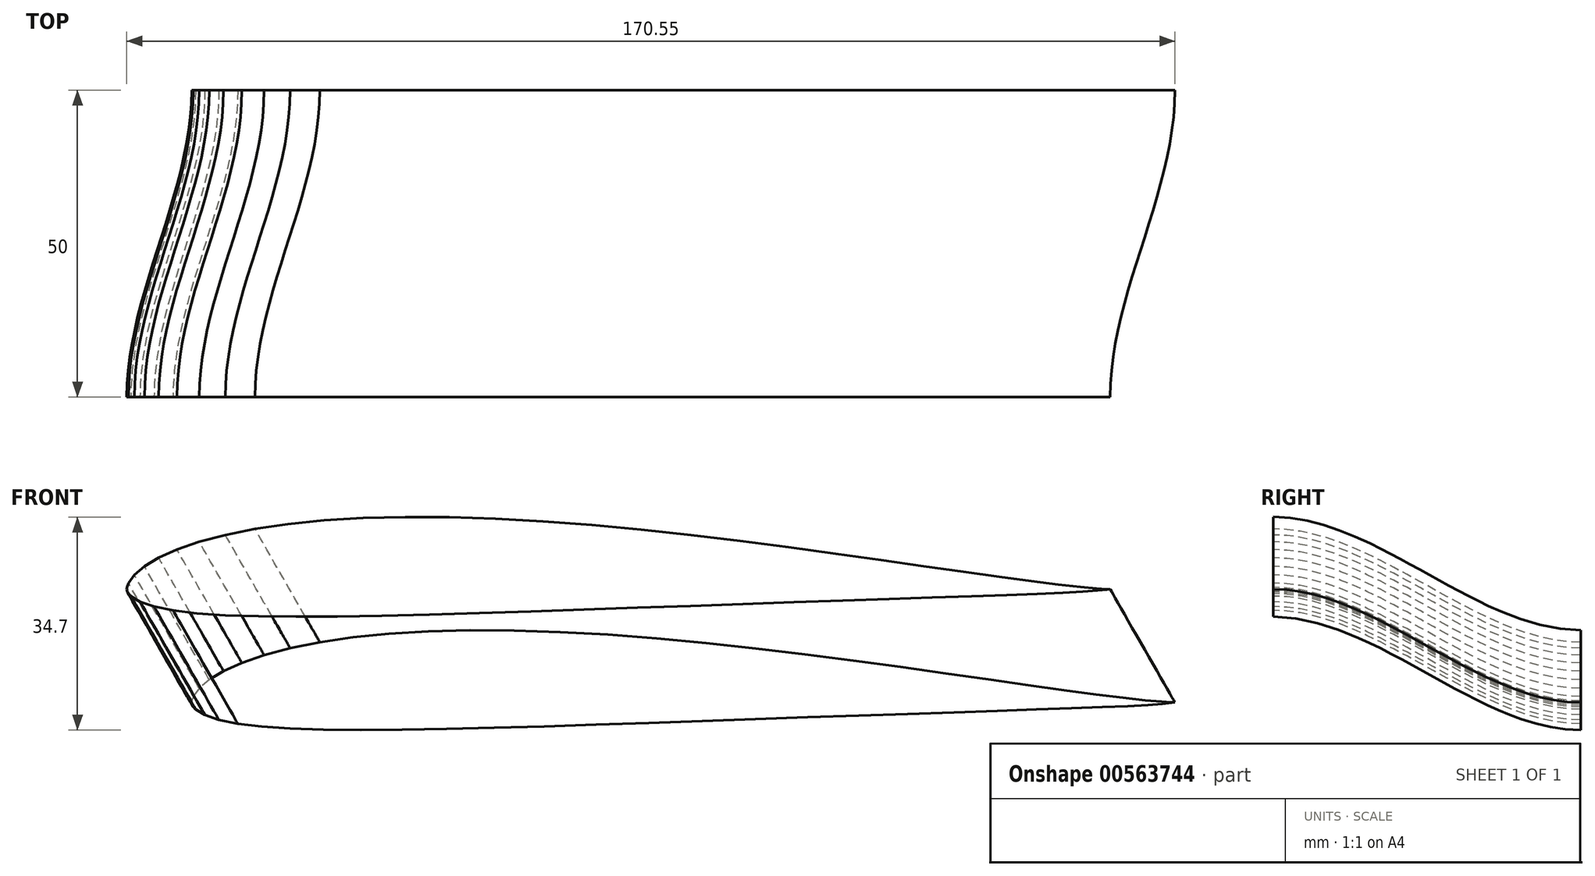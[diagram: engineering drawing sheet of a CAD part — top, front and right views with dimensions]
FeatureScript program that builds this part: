
annotation { "Feature Type Name" : "Feature", "Feature Type Description" : "" }
export const myFeature = defineFeature(function(context is Context, id is Id, definition is map)
    precondition{}
    {
        {
            var Q0;
            Q0=qCreatedBy(makeId("Front.planeOp"),FACE);
            var sketch = newSketch(context, id + "F0", { "sketchPlane" : qUnion([Q0])});
            skLineSegment(sketch, "E0", {"start": v(160, 0) * mm, "end": v(159.44, 0.02) * mm});
            skLineSegment(sketch, "E1", {"start": v(159.44, 0.02) * mm, "end": v(157.8, 0.13) * mm});
            skLineSegment(sketch, "E2", {"start": v(157.8, 0.13) * mm, "end": v(155.15, 0.37) * mm});
            skLineSegment(sketch, "E3", {"start": v(155.15, 0.37) * mm, "end": v(151.57, 0.77) * mm});
            skLineSegment(sketch, "E4", {"start": v(151.57, 0.77) * mm, "end": v(147.15, 1.32) * mm});
            skLineSegment(sketch, "E5", {"start": v(147.15, 1.32) * mm, "end": v(141.96, 2.02) * mm});
            skLineSegment(sketch, "E6", {"start": v(141.96, 2.02) * mm, "end": v(136.1, 2.84) * mm});
            skLineSegment(sketch, "E7", {"start": v(136.1, 2.84) * mm, "end": v(129.65, 3.76) * mm});
            skLineSegment(sketch, "E8", {"start": v(129.65, 3.76) * mm, "end": v(122.7, 4.75) * mm});
            skLineSegment(sketch, "E9", {"start": v(122.7, 4.75) * mm, "end": v(115.35, 5.79) * mm});
            skLineSegment(sketch, "E10", {"start": v(115.35, 5.79) * mm, "end": v(107.68, 6.83) * mm});
            skLineSegment(sketch, "E11", {"start": v(107.68, 6.83) * mm, "end": v(99.8, 7.85) * mm});
            skLineSegment(sketch, "E12", {"start": v(99.8, 7.85) * mm, "end": v(91.77, 8.82) * mm});
            skLineSegment(sketch, "E13", {"start": v(91.77, 8.82) * mm, "end": v(83.69, 9.69) * mm});
            skLineSegment(sketch, "E14", {"start": v(83.69, 9.69) * mm, "end": v(75.64, 10.44) * mm});
            skLineSegment(sketch, "E15", {"start": v(75.64, 10.44) * mm, "end": v(67.7, 11.05) * mm});
            skLineSegment(sketch, "E16", {"start": v(67.7, 11.05) * mm, "end": v(59.96, 11.48) * mm});
            skLineSegment(sketch, "E17", {"start": v(59.96, 11.48) * mm, "end": v(52.46, 11.73) * mm});
            skLineSegment(sketch, "E18", {"start": v(52.46, 11.73) * mm, "end": v(45.28, 11.77) * mm});
            skLineSegment(sketch, "E19", {"start": v(45.28, 11.77) * mm, "end": v(38.48, 11.6) * mm});
            skLineSegment(sketch, "E20", {"start": v(38.48, 11.6) * mm, "end": v(32.12, 11.22) * mm});
            skLineSegment(sketch, "E21", {"start": v(32.12, 11.22) * mm, "end": v(26.23, 10.63) * mm});
            skLineSegment(sketch, "E22", {"start": v(26.23, 10.63) * mm, "end": v(20.86, 9.83) * mm});
            skLineSegment(sketch, "E23", {"start": v(20.86, 9.83) * mm, "end": v(16.04, 8.85) * mm});
            skLineSegment(sketch, "E24", {"start": v(16.04, 8.85) * mm, "end": v(11.8, 7.71) * mm});
            skLineSegment(sketch, "E25", {"start": v(11.8, 7.71) * mm, "end": v(8.18, 6.45) * mm});
            skLineSegment(sketch, "E26", {"start": v(8.18, 6.45) * mm, "end": v(5.2, 5.11) * mm});
            skLineSegment(sketch, "E27", {"start": v(5.2, 5.11) * mm, "end": v(2.87, 3.72) * mm});
            skLineSegment(sketch, "E28", {"start": v(2.87, 3.72) * mm, "end": v(1.23, 2.33) * mm});
            skLineSegment(sketch, "E29", {"start": v(1.23, 2.33) * mm, "end": v(0.27, 1) * mm});
            skLineSegment(sketch, "E30", {"start": v(0.27, 1) * mm, "end": v(0.03, 0.3) * mm});
            skLineSegment(sketch, "E31", {"start": v(0.03, 0.3) * mm, "end": v(0, 0.02) * mm});
            skLineSegment(sketch, "E32", {"start": v(0, 0.02) * mm, "end": v(0.02, -0.23) * mm});
            skLineSegment(sketch, "E33", {"start": v(0.02, -0.23) * mm, "end": v(0.11, -0.47) * mm});
            skLineSegment(sketch, "E34", {"start": v(0.11, -0.47) * mm, "end": v(0.27, -0.71) * mm});
            skLineSegment(sketch, "E35", {"start": v(0.27, -0.71) * mm, "end": v(0.66, -1.13) * mm});
            skLineSegment(sketch, "E36", {"start": v(0.66, -1.13) * mm, "end": v(2.15, -2.03) * mm});
            skLineSegment(sketch, "E37", {"start": v(2.15, -2.03) * mm, "end": v(4.44, -2.82) * mm});
            skLineSegment(sketch, "E38", {"start": v(4.44, -2.82) * mm, "end": v(7.52, -3.45) * mm});
            skLineSegment(sketch, "E39", {"start": v(7.52, -3.45) * mm, "end": v(11.4, -3.92) * mm});
            skLineSegment(sketch, "E40", {"start": v(11.4, -3.92) * mm, "end": v(16.05, -4.23) * mm});
            skLineSegment(sketch, "E41", {"start": v(16.05, -4.23) * mm, "end": v(21.44, -4.42) * mm});
            skLineSegment(sketch, "E42", {"start": v(21.44, -4.42) * mm, "end": v(27.52, -4.48) * mm});
            skLineSegment(sketch, "E43", {"start": v(27.52, -4.48) * mm, "end": v(34.24, -4.43) * mm});
            skLineSegment(sketch, "E44", {"start": v(34.24, -4.43) * mm, "end": v(41.5, -4.31) * mm});
            skLineSegment(sketch, "E45", {"start": v(41.5, -4.31) * mm, "end": v(49.25, -4.12) * mm});
            skLineSegment(sketch, "E46", {"start": v(49.25, -4.12) * mm, "end": v(57.38, -3.88) * mm});
            skLineSegment(sketch, "E47", {"start": v(57.38, -3.88) * mm, "end": v(65.8, -3.61) * mm});
            skLineSegment(sketch, "E48", {"start": v(65.8, -3.61) * mm, "end": v(74.4, -3.32) * mm});
            skLineSegment(sketch, "E49", {"start": v(74.4, -3.32) * mm, "end": v(83.07, -3.01) * mm});
            skLineSegment(sketch, "E50", {"start": v(83.07, -3.01) * mm, "end": v(91.73, -2.7) * mm});
            skLineSegment(sketch, "E51", {"start": v(91.73, -2.7) * mm, "end": v(100.26, -2.4) * mm});
            skLineSegment(sketch, "E52", {"start": v(100.26, -2.4) * mm, "end": v(108.55, -2.12) * mm});
            skLineSegment(sketch, "E53", {"start": v(108.55, -2.12) * mm, "end": v(116.52, -1.85) * mm});
            skLineSegment(sketch, "E54", {"start": v(116.52, -1.85) * mm, "end": v(124.05, -1.6) * mm});
            skLineSegment(sketch, "E55", {"start": v(124.05, -1.6) * mm, "end": v(131.06, -1.36) * mm});
            skLineSegment(sketch, "E56", {"start": v(131.06, -1.36) * mm, "end": v(137.47, -1.14) * mm});
            skLineSegment(sketch, "E57", {"start": v(137.47, -1.14) * mm, "end": v(143.18, -0.94) * mm});
            skLineSegment(sketch, "E58", {"start": v(143.18, -0.94) * mm, "end": v(148.15, -0.75) * mm});
            skLineSegment(sketch, "E59", {"start": v(148.15, -0.75) * mm, "end": v(152.3, -0.58) * mm});
            skLineSegment(sketch, "E60", {"start": v(152.3, -0.58) * mm, "end": v(155.57, -0.4) * mm});
            skLineSegment(sketch, "E61", {"start": v(155.57, -0.4) * mm, "end": v(157.96, -0.22) * mm});
            skLineSegment(sketch, "E62", {"start": v(157.96, -0.22) * mm, "end": v(159.47, -0.06) * mm});
            skLineSegment(sketch, "E63", {"start": v(159.47, -0.06) * mm, "end": v(160, 0) * mm});
            skSolve(sketch);
        }
        {
            var Q0;
            Q0=qCreatedBy(makeId("Front.planeOp"),FACE);
            cPlane(context, id + "F1", {"entities" : qUnion([Q0]), "cplaneType" : CPlaneType.OFFSET, "offset" : 50 * mm, "width" : 150 * mm, "height" : 150 * mm});
        }
        {
            var Q0;
            Q0=qCreatedBy(id+"F1.planeOp",FACE);
            var sketch = newSketch(context, id + "F2", { "sketchPlane" : qUnion([Q0])});
            skLineSegment(sketch, "E64", {"start": v(149.45, 18.45) * mm, "end": v(148.89, 18.47) * mm});
            skLineSegment(sketch, "E65", {"start": v(148.89, 18.47) * mm, "end": v(147.25, 18.58) * mm});
            skLineSegment(sketch, "E66", {"start": v(147.25, 18.58) * mm, "end": v(144.6, 18.82) * mm});
            skLineSegment(sketch, "E67", {"start": v(144.6, 18.82) * mm, "end": v(141.02, 19.22) * mm});
            skLineSegment(sketch, "E68", {"start": v(141.02, 19.22) * mm, "end": v(136.6, 19.77) * mm});
            skLineSegment(sketch, "E69", {"start": v(136.6, 19.77) * mm, "end": v(131.4, 20.47) * mm});
            skLineSegment(sketch, "E70", {"start": v(131.4, 20.47) * mm, "end": v(125.54, 21.29) * mm});
            skLineSegment(sketch, "E71", {"start": v(125.54, 21.29) * mm, "end": v(119.1, 22.21) * mm});
            skLineSegment(sketch, "E72", {"start": v(119.1, 22.21) * mm, "end": v(112.15, 23.2) * mm});
            skLineSegment(sketch, "E73", {"start": v(112.15, 23.2) * mm, "end": v(104.8, 24.24) * mm});
            skLineSegment(sketch, "E74", {"start": v(104.8, 24.24) * mm, "end": v(97.13, 25.28) * mm});
            skLineSegment(sketch, "E75", {"start": v(97.13, 25.28) * mm, "end": v(89.24, 26.3) * mm});
            skLineSegment(sketch, "E76", {"start": v(89.24, 26.3) * mm, "end": v(81.21, 27.27) * mm});
            skLineSegment(sketch, "E77", {"start": v(81.21, 27.27) * mm, "end": v(73.14, 28.14) * mm});
            skLineSegment(sketch, "E78", {"start": v(73.14, 28.14) * mm, "end": v(65.1, 28.9) * mm});
            skLineSegment(sketch, "E79", {"start": v(65.1, 28.9) * mm, "end": v(57.16, 29.5) * mm});
            skLineSegment(sketch, "E80", {"start": v(57.16, 29.5) * mm, "end": v(49.4, 29.93) * mm});
            skLineSegment(sketch, "E81", {"start": v(49.4, 29.93) * mm, "end": v(41.9, 30.18) * mm});
            skLineSegment(sketch, "E82", {"start": v(41.9, 30.18) * mm, "end": v(34.73, 30.22) * mm});
            skLineSegment(sketch, "E83", {"start": v(34.73, 30.22) * mm, "end": v(27.93, 30.06) * mm});
            skLineSegment(sketch, "E84", {"start": v(27.93, 30.06) * mm, "end": v(21.56, 29.67) * mm});
            skLineSegment(sketch, "E85", {"start": v(21.56, 29.67) * mm, "end": v(15.68, 29.08) * mm});
            skLineSegment(sketch, "E86", {"start": v(15.68, 29.08) * mm, "end": v(10.3, 28.28) * mm});
            skLineSegment(sketch, "E87", {"start": v(10.3, 28.28) * mm, "end": v(5.48, 27.3) * mm});
            skLineSegment(sketch, "E88", {"start": v(5.48, 27.3) * mm, "end": v(1.25, 26.16) * mm});
            skLineSegment(sketch, "E89", {"start": v(1.25, 26.16) * mm, "end": v(-2.38, 24.9) * mm});
            skLineSegment(sketch, "E90", {"start": v(-2.38, 24.9) * mm, "end": v(-5.36, 23.56) * mm});
            skLineSegment(sketch, "E91", {"start": v(-5.36, 23.56) * mm, "end": v(-7.68, 22.17) * mm});
            skLineSegment(sketch, "E92", {"start": v(-7.68, 22.17) * mm, "end": v(-9.32, 20.78) * mm});
            skLineSegment(sketch, "E93", {"start": v(-9.32, 20.78) * mm, "end": v(-10.28, 19.45) * mm});
            skLineSegment(sketch, "E94", {"start": v(-10.28, 19.45) * mm, "end": v(-10.52, 18.75) * mm});
            skLineSegment(sketch, "E95", {"start": v(-10.52, 18.75) * mm, "end": v(-10.55, 18.47) * mm});
            skLineSegment(sketch, "E96", {"start": v(-10.55, 18.47) * mm, "end": v(-10.53, 18.22) * mm});
            skLineSegment(sketch, "E97", {"start": v(-10.53, 18.22) * mm, "end": v(-10.44, 17.98) * mm});
            skLineSegment(sketch, "E98", {"start": v(-10.44, 17.98) * mm, "end": v(-10.28, 17.74) * mm});
            skLineSegment(sketch, "E99", {"start": v(-10.28, 17.74) * mm, "end": v(-9.9, 17.32) * mm});
            skLineSegment(sketch, "E100", {"start": v(-9.9, 17.32) * mm, "end": v(-8.4, 16.42) * mm});
            skLineSegment(sketch, "E101", {"start": v(-8.4, 16.42) * mm, "end": v(-6.11, 15.63) * mm});
            skLineSegment(sketch, "E102", {"start": v(-6.11, 15.63) * mm, "end": v(-3.03, 15) * mm});
            skLineSegment(sketch, "E103", {"start": v(-3.03, 15) * mm, "end": v(0.84, 14.53) * mm});
            skLineSegment(sketch, "E104", {"start": v(0.84, 14.53) * mm, "end": v(5.5, 14.22) * mm});
            skLineSegment(sketch, "E105", {"start": v(5.5, 14.22) * mm, "end": v(10.89, 14.03) * mm});
            skLineSegment(sketch, "E106", {"start": v(10.89, 14.03) * mm, "end": v(16.97, 13.98) * mm});
            skLineSegment(sketch, "E107", {"start": v(16.97, 13.98) * mm, "end": v(23.68, 14.02) * mm});
            skLineSegment(sketch, "E108", {"start": v(23.68, 14.02) * mm, "end": v(30.96, 14.14) * mm});
            skLineSegment(sketch, "E109", {"start": v(30.96, 14.14) * mm, "end": v(38.7, 14.33) * mm});
            skLineSegment(sketch, "E110", {"start": v(38.7, 14.33) * mm, "end": v(46.83, 14.57) * mm});
            skLineSegment(sketch, "E111", {"start": v(46.83, 14.57) * mm, "end": v(55.24, 14.84) * mm});
            skLineSegment(sketch, "E112", {"start": v(55.24, 14.84) * mm, "end": v(63.84, 15.13) * mm});
            skLineSegment(sketch, "E113", {"start": v(63.84, 15.13) * mm, "end": v(72.52, 15.44) * mm});
            skLineSegment(sketch, "E114", {"start": v(72.52, 15.44) * mm, "end": v(81.18, 15.74) * mm});
            skLineSegment(sketch, "E115", {"start": v(81.18, 15.74) * mm, "end": v(89.7, 16.04) * mm});
            skLineSegment(sketch, "E116", {"start": v(89.7, 16.04) * mm, "end": v(98, 16.33) * mm});
            skLineSegment(sketch, "E117", {"start": v(98, 16.33) * mm, "end": v(105.96, 16.6) * mm});
            skLineSegment(sketch, "E118", {"start": v(105.96, 16.6) * mm, "end": v(113.5, 16.86) * mm});
            skLineSegment(sketch, "E119", {"start": v(113.5, 16.86) * mm, "end": v(120.51, 17.1) * mm});
            skLineSegment(sketch, "E120", {"start": v(120.51, 17.1) * mm, "end": v(126.92, 17.3) * mm});
            skLineSegment(sketch, "E121", {"start": v(126.92, 17.3) * mm, "end": v(132.63, 17.5) * mm});
            skLineSegment(sketch, "E122", {"start": v(132.63, 17.5) * mm, "end": v(137.6, 17.7) * mm});
            skLineSegment(sketch, "E123", {"start": v(137.6, 17.7) * mm, "end": v(141.74, 17.87) * mm});
            skLineSegment(sketch, "E124", {"start": v(141.74, 17.87) * mm, "end": v(145.02, 18.05) * mm});
            skLineSegment(sketch, "E125", {"start": v(145.02, 18.05) * mm, "end": v(147.41, 18.23) * mm});
            skLineSegment(sketch, "E126", {"start": v(147.41, 18.23) * mm, "end": v(148.92, 18.39) * mm});
            skLineSegment(sketch, "E127", {"start": v(148.92, 18.39) * mm, "end": v(149.45, 18.45) * mm});
            skSolve(sketch);
        }
        {
            var Q0;
            Q0 = qSketchRegion(id + "F0", true);
            var Q1;
            Q1 = qSketchRegion(id + "F2", true);
            loft(context, id + "F3", {"startCondition" : LoftEndDerivativeType.NORMAL_TO_PROFILE, "startMagnitude" : 1, "endCondition" : LoftEndDerivativeType.NORMAL_TO_PROFILE, "endMagnitude" : 1, "sheetProfilesArray" : [{ "sheetProfileEntities" : qUnion([Q0]) }, { "sheetProfileEntities" : qUnion([Q1]) }]});
        }
    });
